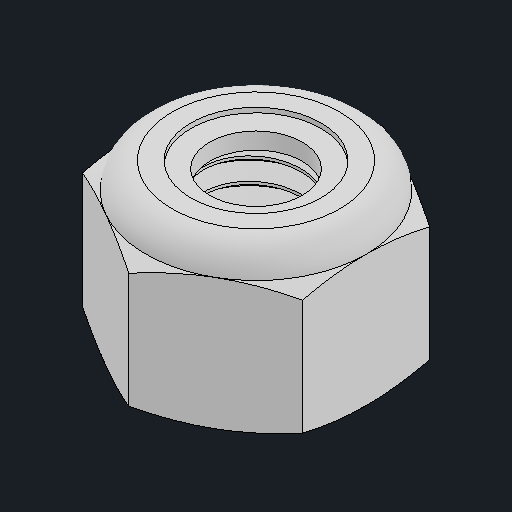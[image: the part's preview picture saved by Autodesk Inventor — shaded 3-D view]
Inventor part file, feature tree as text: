
AUTODESK INVENTOR PART (.ipt)
format: ipt  version: 2024.2 (Build 282272000, 272)  size: 334,848 bytes
history: native  units: mm
features: other x3, revolve x1
ambient origin geometry x8: Origin, YZ Plane, XZ Plane, XY Plane, X Axis, Y Axis, Z Axis, Center Point
bodies: Body1 (feature_tree), Body2 (feature_tree)
feature tree (4):
  other  "솔리드1"
  other  "솔리드2"
  other  "Cut-Revolve4"
  revolve  "Revolve2"  [1 undecoded]
note: 1 required parameter value undecoded (feature->parameter linkage not recoverable at this tier; creation-order binding heuristic only, values carry confidence <= 0.55)
